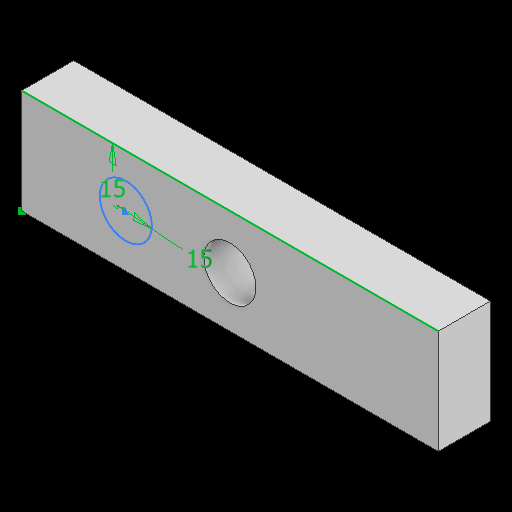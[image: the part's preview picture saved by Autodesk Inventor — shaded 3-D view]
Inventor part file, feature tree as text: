
AUTODESK INVENTOR PART (.ipt)
format: ipt  version: 2025.1 (Build 291241000, 241)  size: 102,400 bytes
history: native  units: in
note: dims shown in document units (in); Inventor stores cm internally (conversion verified against a paired STEP export)
features: sketch x3, extrude x2, other x1
ambient origin geometry x8: Origin, YZ Plane, XZ Plane, XY Plane, X Axis, Y Axis, Z Axis, Center Point
bodies: Body1 (feature_tree)
feature tree (6):
  other  "솔리드1"
  extrude  "돌출1"  Depth=4.7244in
  sketch  "스케치2"
  extrude  "돌출2"  Depth=1.1811in
  sketch  "스케치1"
  sketch  "스케치3"
